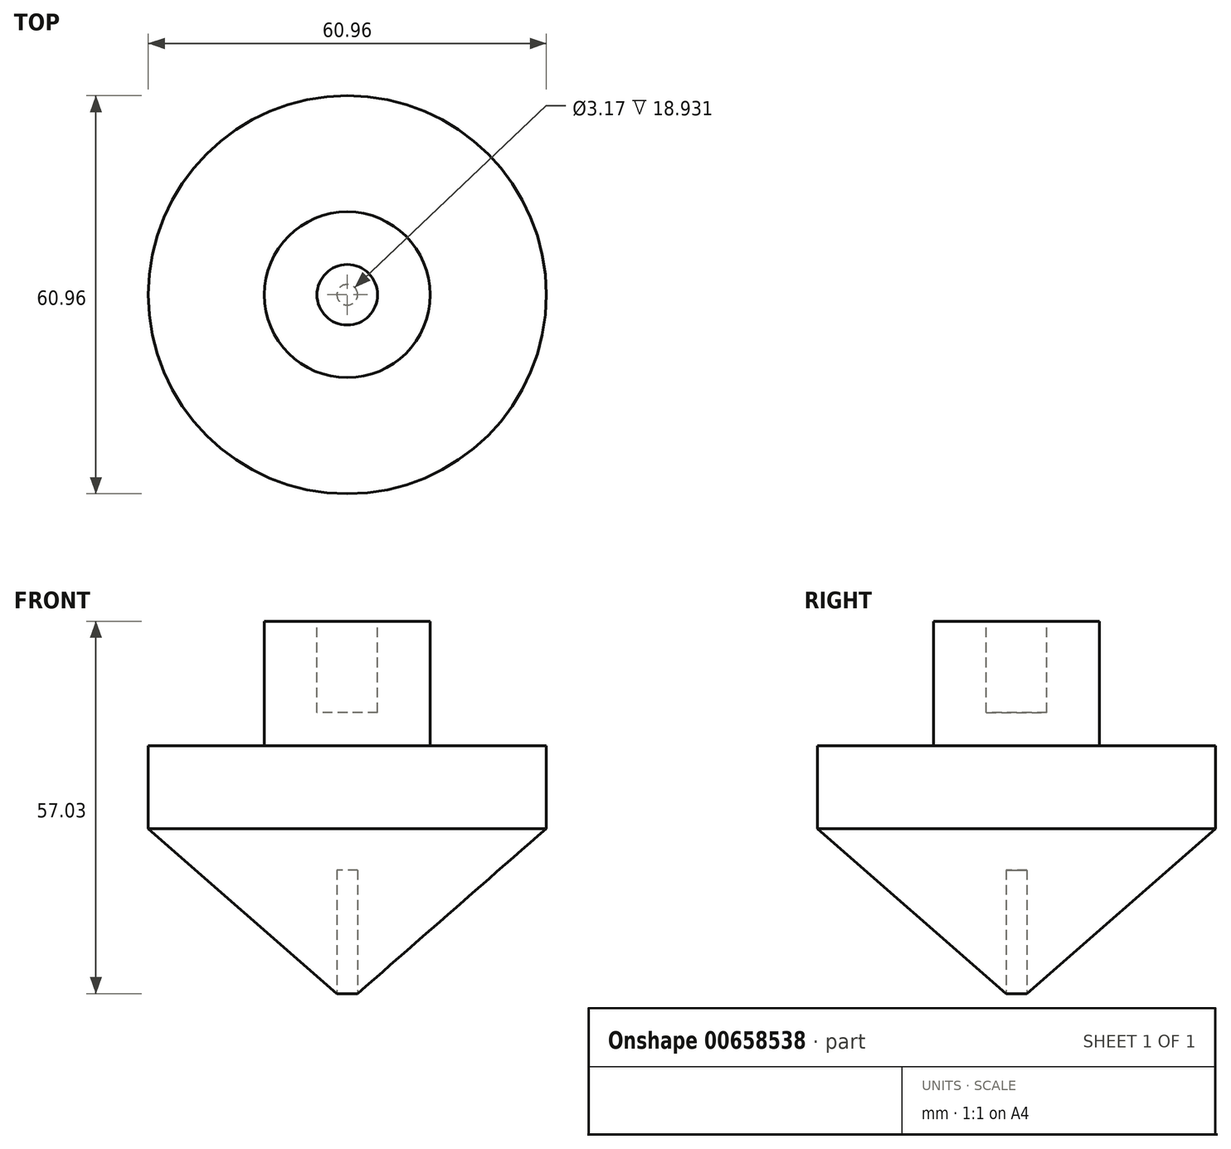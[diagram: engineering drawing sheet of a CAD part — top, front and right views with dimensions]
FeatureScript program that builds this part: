
annotation { "Feature Type Name" : "Feature", "Feature Type Description" : "" }
export const myFeature = defineFeature(function(context is Context, id is Id, definition is map)
    precondition{}
    {
        {
            var Q0;
            Q0=qCreatedBy(makeId("Front.planeOp"),FACE);
            var sketch = newSketch(context, id + "F0", { "sketchPlane" : qUnion([Q0])});
            skLineSegment(sketch, "E0", {"start": v(0, 0) * mm, "end": v(30.48, 26.67) * mm});
            skLineSegment(sketch, "E1", {"start": v(30.48, 26.67) * mm, "end": v(30.48, 39.37) * mm});
            skLineSegment(sketch, "E2", {"start": v(30.48, 39.37) * mm, "end": v(12.7, 39.37) * mm});
            skLineSegment(sketch, "E3", {"start": v(12.7, 39.37) * mm, "end": v(12.7, 58.42) * mm});
            skLineSegment(sketch, "E4", {"start": v(12.7, 58.42) * mm, "end": v(0, 58.42) * mm});
            skLineSegment(sketch, "E5", {"start": v(0, 58.42) * mm, "end": v(0, 0) * mm});
            skSolve(sketch);
        }
        {
            var Q0;
            Q0=qSketchRegion(id+"F0",true);
            var Q1;
            Q1=sQuery(id+"F0.wireOp",EDGE,"E5");
            revolve(context, id + "F1", {"entities" : qUnion([Q0]), "axis" : qUnion([Q1]), "revolveType" : RevolveType.FULL});
        }
        {
            var Q0;
            Q0=makeQuery(id+"F1.opRevolve","SWEPT_FACE",FACE,{"disambiguationData":[OSD([sQuery(id+"F0.wireOp",EDGE,"E4")])]});
            var sketch = newSketch(context, id + "F2", { "sketchPlane" : qUnion([Q0])});
            skCircle(sketch, "E6", {"center": v(0, 0) * mm, "radius": 4.64 * mm});
            skSolve(sketch);
        }
        {
            var Q0;
            Q0=qSketchRegion(id+"F2",true);
            extrude(context, id + "F3", {"entities" : qUnion([Q0]), "operationType" : NewBodyOperationType.REMOVE, "oppositeDirection" : true, "depth" : 13.97 * mm, "offsetDistance" : 25.4 * mm});
        }
        {
            var Q0;
            Q0=qCreatedBy(makeId("Top.planeOp"),FACE);
            var sketch = newSketch(context, id + "F4", { "sketchPlane" : qUnion([Q0])});
            skCircle(sketch, "E7", {"center": v(0, 0) * mm, "radius": 1.59 * mm});
            skSolve(sketch);
        }
        {
            var Q0;
            Q0=qSketchRegion(id+"F4",true);
            extrude(context, id + "F5", {"entities" : qUnion([Q0]), "operationType" : NewBodyOperationType.REMOVE, "depth" : 20.32 * mm, "offsetDistance" : 25.4 * mm});
        }
    });
